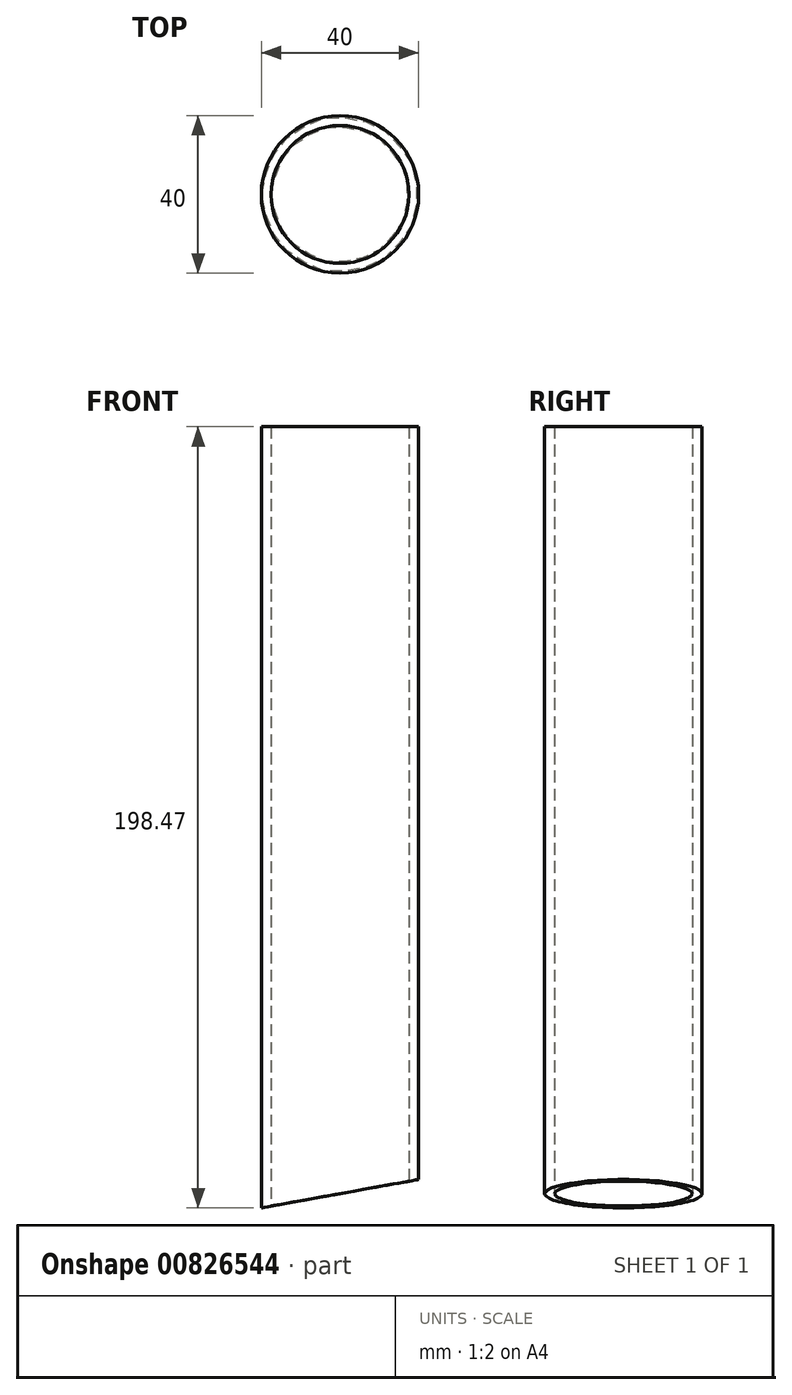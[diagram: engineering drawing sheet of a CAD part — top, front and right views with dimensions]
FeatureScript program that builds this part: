
annotation { "Feature Type Name" : "Feature", "Feature Type Description" : "" }
export const myFeature = defineFeature(function(context is Context, id is Id, definition is map)
    precondition{}
    {
        {
            var Q0;
            Q0=qCreatedBy(makeId("Top.planeOp"),FACE);
            var sketch = newSketch(context, id + "F0", { "sketchPlane" : qUnion([Q0])});
            skCircle(sketch, "E0", {"center": v(0, 0) * mm, "radius": 20 * mm});
            skCircle(sketch, "E1", {"center": v(0, 0) * mm, "radius": 17.5 * mm});
            skSolve(sketch);
        }
        {
            var Q0;
            Q0=makeQuery(id+"F0.imprint","IMPRINT",FACE,{"disambiguationData":[TD([[makeQuery(id+"F0.imprint","IMPRINT",EDGE,{"derivedFrom":sQuery(id+"F0.wireOp",EDGE,"E0")}),1.0]])]});
            extrude(context, id + "F1", {"entities" : qUnion([Q0]), "depth" : (180 + 18 + 0.47) * mm, "offsetDistance" : 25 * mm});
        }
        {
            var Q0;
            Q0=qCreatedBy(makeId("Front.planeOp"),FACE);
            var sketch = newSketch(context, id + "F2", { "sketchPlane" : qUnion([Q0])});
            skLineSegment(sketch, "E2", {"start": v(-20, 0) * mm, "end": v(0, 0) * mm});
            skLineSegment(sketch, "E3", {"start": v(0, 0) * mm, "end": v(20, 0) * mm});
            skLineSegment(sketch, "E4", {"start": v(20, 0) * mm, "end": v(20, 19.08) * mm});
            skLineSegment(sketch, "E5", {"start": v(-20, 0) * mm, "end": v(20, 7.2) * mm});
            skSolve(sketch);
        }
        {
            var Q0;
            Q0 = qSketchRegion(id + "F2", true);
            extrude(context, id + "F3", {"entities" : qUnion([Q0]), "operationType" : NewBodyOperationType.REMOVE, "endBound" : BoundingType.SYMMETRIC, "oppositeDirection" : true, "depth" : 50 * mm, "offsetDistance" : 25 * mm});
        }
    });
